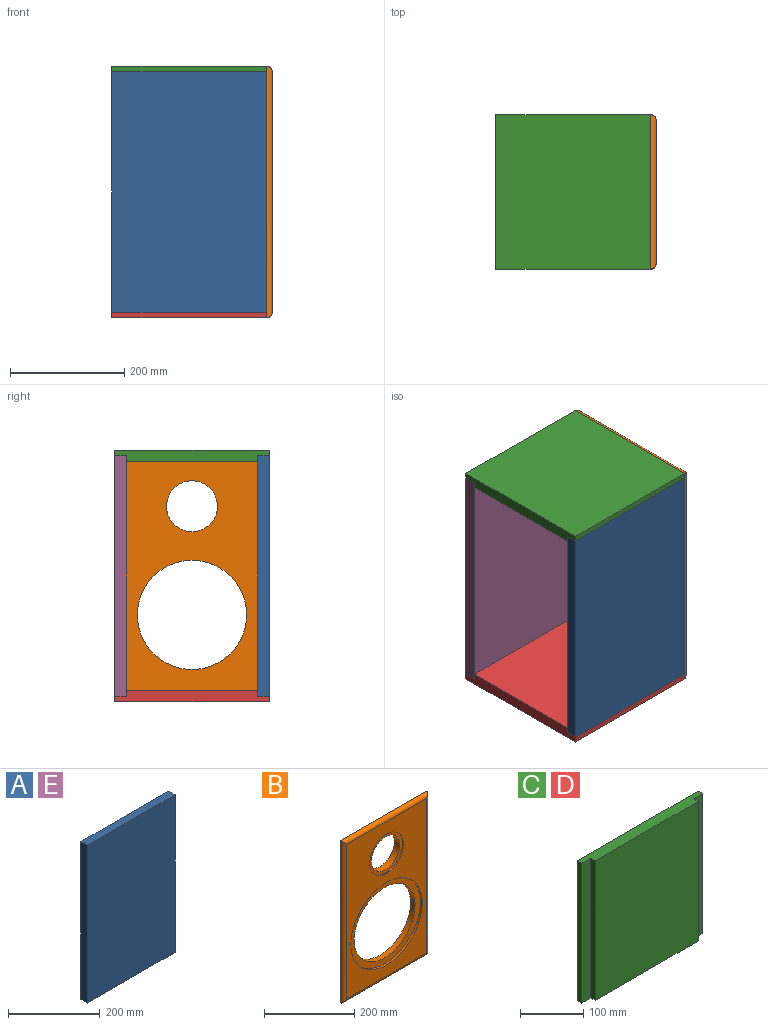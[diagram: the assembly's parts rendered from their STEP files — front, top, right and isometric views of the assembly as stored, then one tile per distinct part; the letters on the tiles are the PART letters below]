
ASSEMBLY  parts=5 mates=5
PART A: 6 faces, bbox 270x20x420 mm
  f0: plane 420x20mm, normal (-1,0,0), area 8400mm2, adj f1,f3,f4,f5
  f1: plane 270x20mm, normal (0,0,-1), area 5400mm2, adj f0,f2,f4,f5
  f2: plane 420x20mm, normal (1,0,0), area 8400mm2, adj f1,f3,f4,f5
  f3: plane 270x20mm, normal (0,0,1), area 5400mm2, adj f0,f2,f4,f5
  f4: plane 420x270mm, normal (0,-1,0), area 113400mm2, adj f0,f1,f2,f3
  f5: plane 420x270mm, normal (0,1,0), area 113400mm2, adj f0,f1,f2,f3
PART B: 17 faces, bbox 270x20x440 mm
  f0: plane 400x240mm, normal (0,1,0), area 61126.8mm2, adj f4,f7,f8,f9,f10,f11
  f1: plane 420x250mm, normal (0,-1,0), area 56767.1mm2, adj f2,f5,f13,f14,f15,f16
  f2: cylinder r=112mm len=224mm, axis (0,-1,0), area 4222.3mm2, adj f1,f3
  f3: plane 224x224mm, normal (0,-1,0), area 10756mm2, adj f2,f4
  f4: cylinder r=95.5mm len=191mm, axis (0,-1,0), area 8400.6mm2, adj f0,f3
  f5: cylinder r=53mm len=106mm, axis (0,-1,0), area 999mm2, adj f1,f6
  f6: plane 106x106mm, normal (0,-1,0), area 2603.6mm2, adj f5,f7
  f7: cylinder r=44.5mm len=89mm, axis (0,-1,0), area 4753.2mm2, adj f0,f6
  f8: plane 400x10mm, normal (1,0,0), area 4000mm2, adj f0,f9,f11,f12
  f9: plane 240x10mm, normal (0,0,1), area 2400mm2, adj f0,f8,f10,f12
  f10: plane 400x10mm, normal (-1,0,0), area 4000mm2, adj f0,f9,f11,f12
  f11: plane 240x10mm, normal (0,0,-1), area 2400mm2, adj f0,f8,f10,f12
  f12: plane 440x270mm, normal (0,1,0), area 22800mm2, adj f8,f9,f10,f11,f13,f14,f15,f16
  f13: cylinder r=10mm len=440mm, axis (0,0,1), area 6797.3mm2, adj f1,f12,f14,f15
  f14: cylinder r=10mm len=270mm, axis (-1,0,0), area 4127mm2, adj f1,f12,f13,f16
  f15: cylinder r=10mm len=270mm, axis (1,0,0), area 4127mm2, adj f1,f12,f13,f16
  f16: cylinder r=10mm len=440mm, axis (0,0,-1), area 6797.3mm2, adj f1,f12,f14,f15
PART C: 10 faces, bbox 270x20x270 mm
  f0: plane 270x20mm, normal (0,0,1), area 5000mm2, adj f1,f2,f3,f5,f6,f7,f8,f9
  f1: plane 270x230mm, normal (0,-1,0), area 62100mm2, adj f0,f4,f6,f8
  f2: plane 270x10mm, normal (1,0,0), area 2700mm2, adj f0,f4,f5,f9
  f3: plane 270x10mm, normal (-1,0,0), area 2700mm2, adj f0,f4,f5,f7
  f4: plane 270x20mm, normal (0,0,-1), area 5000mm2, adj f1,f2,f3,f5,f6,f7,f8,f9
  f5: plane 270x270mm, normal (0,1,0), area 72900mm2, adj f0,f2,f3,f4
  f6: plane 270x10mm, normal (-1,0,0), area 2700mm2, adj f0,f1,f4,f7
  f7: plane 270x20mm, normal (0,-1,0), area 5400mm2, adj f0,f3,f4,f6
  f8: plane 270x10mm, normal (1,0,0), area 2700mm2, adj f0,f1,f4,f9
  f9: plane 270x20mm, normal (0,-1,0), area 5400mm2, adj f0,f2,f4,f8
PART D: same geometry as C
PART E: same geometry as A
PLACE A t=(201.16,193.43,155.03)mm
PLACE B rot(axis=(0,0,1),90deg) t=(326.16,308.43,155.03)mm
PLACE C rot(axis=(0.58,-0.58,-0.58),120deg) t=(201.16,308.43,375.03)mm
PLACE D rot(axis=(-0.58,0.58,-0.58),120deg) t=(201.16,308.43,-64.97)mm
PLACE E t=(201.16,443.43,155.03)mm
MATE fastened C.f2 <-> A.f4  axis (0,-1,0) through (201.16,173.43,365.03)mm
MATE fastened E.f4 <-> C.f6  axis (0,-1,0) through (201.16,423.43,365.03)mm
MATE parallel E.f1 <-> D.f7  axis (0,0,-1) through (201.16,433.43,-54.97)mm
MATE fastened E.f1 <-> D.f7  axis (0,0,-1) through (201.16,443.43,-54.97)mm
MATE fastened B.f12 <-> C.f4  axis (-1,0,0) through (336.16,308.43,375.03)mm
